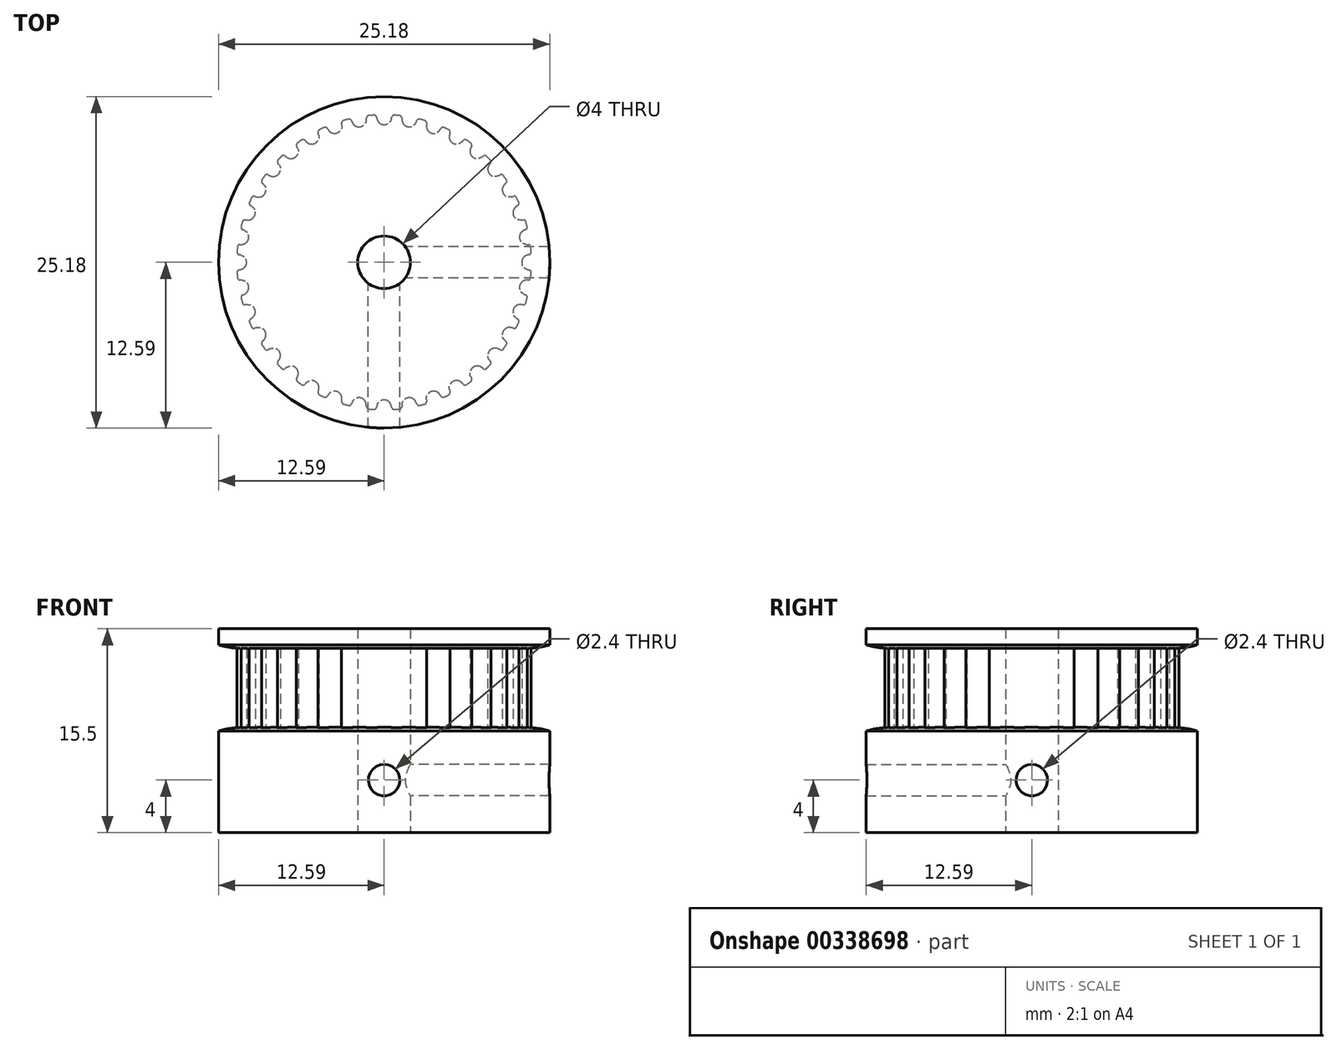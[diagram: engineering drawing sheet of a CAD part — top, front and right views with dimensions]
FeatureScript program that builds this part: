
annotation { "Feature Type Name" : "Feature", "Feature Type Description" : "" }
export const myFeature = defineFeature(function(context is Context, id is Id, definition is map)
    precondition{}
    {
        {
            assignVariable(context, id + "F0", {"name" : "teeth", "anyValue" : 36});
        }
        {
            assignVariable(context, id + "F1", {"name" : "belt_width", "anyValue" : 6 * mm});
        }
        {
            assignVariable(context, id + "F2", {"name" : "bore_diameter", "anyValue" : 4 * mm});
        }
        {
            var Q0;
            Q0=qCreatedBy(makeId("Top.planeOp"),FACE);
            var sketch = newSketch(context, id + "F3", { "sketchPlane" : qUnion([Q0])});
            skLineSegment(sketch, "E0", {"start": v(0, 0) * mm, "end": v(0, 10.46) * mm, "construction": true});
            skCircle(sketch, "E1", {"center": v(0, 0) * mm, "radius": 11.2 * mm});
            skPoint(sketch, "E2.MirrorCS.end.orphan", {"position": v(0.98, 11.16) * mm});
            skLineSegment(sketch, "E3", {"start": v(0.98, 11.16) * mm, "end": v(1, 11.42) * mm, "construction": true});
            skLineSegment(sketch, "E4", {"start": v(-0.98, 11.16) * mm, "end": v(-1, 11.42) * mm, "construction": true});
            skArc(sketch, "E5", {"start": v(0, 10.46) * mm, "mid": v(0.34, 10.57) * mm, "end": v(0.53, 10.86) * mm});
            skArc(sketch, "E6", {"start": v(0.53, 10.86) * mm, "mid": v(0.56, 10.96) * mm, "end": v(0.58, 11.05) * mm, "construction": true});
            skLineSegment(sketch, "E7", {"start": v(0, 10.46) * mm, "end": v(0, 11.2) * mm, "construction": true});
            skLineSegment(sketch, "E8", {"start": v(0, 11.2) * mm, "end": v(0, 11.46) * mm, "construction": true});
            skArc(sketch, "E9", {"start": v(0.58, 11.05) * mm, "mid": v(0.64, 11.15) * mm, "end": v(0.74, 11.18) * mm, "construction": true});
            skArc(sketch, "E10", {"start": v(1, 11.42) * mm, "mid": v(0, 11.46) * mm, "end": v(-1, 11.42) * mm, "construction": true});
            skLineSegment(sketch, "E11", {"start": v(0.98, 11.16) * mm, "end": v(0.91, 10.42) * mm});
            skLineSegment(sketch, "E12", {"start": v(0.91, 10.42) * mm, "end": v(0, 0) * mm});
            skLineSegment(sketch, "E13", {"start": v(0, 0) * mm, "end": v(-0.91, 10.42) * mm});
            skLineSegment(sketch, "E14", {"start": v(-0.91, 10.42) * mm, "end": v(-0.98, 11.16) * mm});
            skArc(sketch, "E15", {"start": v(0.78, 11.18) * mm, "mid": v(0.65, 11.14) * mm, "end": v(0.58, 11.04) * mm});
            skArc(sketch, "E16", {"start": v(0.53, 10.86) * mm, "mid": v(0.56, 10.95) * mm, "end": v(0.58, 11.04) * mm});
            skArc(sketch, "E17.MirrorCS", {"start": v(0, 10.46) * mm, "mid": v(-0.34, 10.57) * mm, "end": v(-0.53, 10.86) * mm});
            skArc(sketch, "E18.MirrorCS", {"start": v(-0.53, 10.86) * mm, "mid": v(-0.56, 10.95) * mm, "end": v(-0.58, 11.04) * mm});
            skArc(sketch, "E19.MirrorCS", {"start": v(-0.78, 11.18) * mm, "mid": v(-0.65, 11.14) * mm, "end": v(-0.58, 11.04) * mm});
            skArc(sketch, "E20", {"start": v(0, 11.2) * mm, "mid": v(-0.2, 11.2) * mm, "end": v(-0.4, 11.2) * mm});
            skArc(sketch, "E21", {"start": v(0.91, 10.42) * mm, "mid": v(0, 10.46) * mm, "end": v(-0.91, 10.42) * mm, "construction": true});
            skLineSegment(sketch, "E22", {"start": v(1, 11.42) * mm, "end": v(1.03, 11.8) * mm, "construction": true});
            skLineSegment(sketch, "E23", {"start": v(-1, 11.42) * mm, "end": v(-1.03, 11.8) * mm, "construction": true});
            skArc(sketch, "E24", {"start": v(-1.03, 11.8) * mm, "mid": v(0, 11.84) * mm, "end": v(1.03, 11.8) * mm, "construction": true});
            skSolve(sketch);
        }
        {
            var Q0;
            Q0=makeQuery(id+"F3.imprint","IMPRINT",FACE,{"disambiguationData":[TD([[makeQuery(id+"F3.imprint","IMPRINT",EDGE,{"derivedFrom":sQuery(id+"F3.wireOp",EDGE,"E5")}),-1.0]])]});
            var Q1;
            {var subQ1=sQuery(id+"F3.wireOp",EDGE,"E14");Q1=makeQuery(id+"F3.imprint","IMPRINT",FACE,{"disambiguationData":[TD([[makeQuery(id+"F3.imprint","IMPRINT",EDGE,{"derivedFrom":subQ1}),-1.0]])]});}
            var Q2;
            {var subQ0=sQuery(id+"F3.wireOp",EDGE,"E12");Q2=makeQuery(id+"F3.imprint","IMPRINT",FACE,{"disambiguationData":[TD([[makeQuery(id+"F3.imprint","IMPRINT",EDGE,{"derivedFrom":subQ0}),-1.0]])]});}
            extrude(context, id + "F4", {"entities" : qUnion([Q0, Q1, Q2]), "endBound" : BoundingType.SYMMETRIC, "depth" : getVariable(context, 'belt_width')});
        }
        {
            var Q0;
            Q0=makeQuery(id+"F4.opExtrude","SWEPT_BODY",BODY,{"disambiguationData":[OSD([sQuery(id+"F3.wireOp",EDGE,"E1"),sQuery(id+"F3.wireOp",EDGE,"E5"),sQuery(id+"F3.wireOp",EDGE,"E11"),sQuery(id+"F3.wireOp",EDGE,"E12"),sQuery(id+"F3.wireOp",EDGE,"E13"),sQuery(id+"F3.wireOp",EDGE,"E14"),sQuery(id+"F3.wireOp",EDGE,"E15"),sQuery(id+"F3.wireOp",EDGE,"E16"),sQuery(id+"F3.wireOp",EDGE,"E17.MirrorCS"),sQuery(id+"F3.wireOp",EDGE,"E18.MirrorCS"),sQuery(id+"F3.wireOp",EDGE,"E19.MirrorCS")])]});
            var Q1;
            Q1=makeQuery(id+"F4.opExtrude","SWEPT_EDGE",EDGE,{"disambiguationData":[OSD([sQuery(id+"F3.wireOp",EDGE,"E12"),sQuery(id+"F3.wireOp",EDGE,"E13")])]});
            circularPattern(context, id + "F5", {"operationType" : NewBodyOperationType.ADD, "entities" : qUnion([Q0]), "axis" : qUnion([Q1]), "angle" : 360 * degree, "instanceCount" : getVariable(context, 'teeth'), "equalSpace" : true});
        }
        {
            var Q0;
            Q0=qCreatedBy(makeId("Front.planeOp"),FACE);
            var sketch = newSketch(context, id + "F6", { "sketchPlane" : qUnion([Q0])});
            skLineSegment(sketch, "E25", {"start": v(0, -3) * mm, "end": v(11.84, -3) * mm});
            skLineSegment(sketch, "E26", {"start": v(11.84, -3) * mm, "end": v(12.6, -3.28) * mm});
            skLineSegment(sketch, "E27", {"start": v(12.6, -3.28) * mm, "end": v(12.6, -11) * mm});
            skLineSegment(sketch, "E28", {"start": v(12.6, -11) * mm, "end": v(0, -11) * mm});
            skLineSegment(sketch, "E29", {"start": v(0, -11) * mm, "end": v(0, -3) * mm});
            skLineSegment(sketch, "E30", {"start": v(0, 3) * mm, "end": v(11.84, 3) * mm});
            skLineSegment(sketch, "E31", {"start": v(12.6, 3.28) * mm, "end": v(11.84, 3) * mm});
            skLineSegment(sketch, "E32", {"start": v(12.6, 3.28) * mm, "end": v(12.6, 4.5) * mm});
            skLineSegment(sketch, "E33", {"start": v(12.6, 4.5) * mm, "end": v(0, 4.5) * mm});
            skLineSegment(sketch, "E34", {"start": v(0, 4.5) * mm, "end": v(0, 3) * mm});
            skLineSegment(sketch, "E35", {"start": v(11.84, -3) * mm, "end": v(12.6, -3) * mm, "construction": true});
            skLineSegment(sketch, "E36", {"start": v(12.6, -3) * mm, "end": v(12.6, -3.28) * mm, "construction": true});
            skLineSegment(sketch, "E37", {"start": v(11.84, 3) * mm, "end": v(12.6, 3) * mm, "construction": true});
            skLineSegment(sketch, "E38", {"start": v(12.6, 3) * mm, "end": v(12.6, 3.28) * mm, "construction": true});
            skLineSegment(sketch, "E39", {"start": v(11.2, 0) * mm, "end": v(11.2, -3) * mm, "construction": true});
            skSolve(sketch);
        }
        {
            var Q0;
            Q0=qSketchRegion(id+"F6",true);
            var Q1;
            Q1=qConstructionFilter(qBodyType(qCreatedBy(id+"F6",EDGE),BodyType.WIRE),ConstructionObject.NO);
            var Q2;
            Q2=sQuery(id+"F6.wireOp",EDGE,"E29");
            revolve(context, id + "F7", {"operationType" : NewBodyOperationType.ADD, "entities" : qUnion([Q0]), "surfaceEntities" : qUnion([Q1]), "axis" : qUnion([Q2]), "revolveType" : RevolveType.FULL});
        }
        {
            var Q0;
            Q0=makeQuery(id+"F7.opRevolve","SWEPT_FACE",FACE,{"disambiguationData":[OSD([sQuery(id+"F6.wireOp",EDGE,"E28")])]});
            var sketch = newSketch(context, id + "F8", { "sketchPlane" : qUnion([Q0])});
            skPoint(sketch, "E40", {"position": v(0, 0) * mm});
            skSolve(sketch);
        }
        {
            var Q0;
            Q0=sQuery(id+"F8.wireOp",VERTEX,"E40");
            var Q1;
            Q1=makeQuery(id+"F4.opExtrude","SWEPT_BODY",BODY,{"disambiguationData":[OSD([sQuery(id+"F3.wireOp",EDGE,"E1"),sQuery(id+"F3.wireOp",EDGE,"E5"),sQuery(id+"F3.wireOp",EDGE,"E11"),sQuery(id+"F3.wireOp",EDGE,"E12"),sQuery(id+"F3.wireOp",EDGE,"E13"),sQuery(id+"F3.wireOp",EDGE,"E14"),sQuery(id+"F3.wireOp",EDGE,"E15"),sQuery(id+"F3.wireOp",EDGE,"E16"),sQuery(id+"F3.wireOp",EDGE,"E17.MirrorCS"),sQuery(id+"F3.wireOp",EDGE,"E18.MirrorCS"),sQuery(id+"F3.wireOp",EDGE,"E19.MirrorCS")])]});
            hole(context, id + "F9", {"style" : HoleStyle.SIMPLE, "holeDiameter" : getVariable(context, 'bore_diameter'), "endStyle" : HoleEndStyle.THROUGH, "locations" : qUnion([Q0]), "scope" : qUnion([Q1]), "isTappedThrough" : true});
        }
        {
            var Q0;
            Q0=qCreatedBy(makeId("Front.planeOp"),FACE);
            var sketch = newSketch(context, id + "F10", { "sketchPlane" : qUnion([Q0])});
            skPoint(sketch, "E41", {"position": v(0, -7) * mm});
            skLineSegment(sketch, "E42", {"start": v(0, -11) * mm, "end": v(0, -3) * mm});
            skSolve(sketch);
        }
        {
            var Q0;
            Q0=qCreatedBy(makeId("Right.planeOp"),FACE);
            var sketch = newSketch(context, id + "F11", { "sketchPlane" : qUnion([Q0])});
            skPoint(sketch, "E43", {"position": v(0, -7) * mm});
            skSolve(sketch);
        }
        {
            var Q0;
            Q0=sQuery(id+"F10.wireOp",VERTEX,"E41");
            var Q1;
            Q1=makeQuery(id+"F4.opExtrude","SWEPT_BODY",BODY,{"disambiguationData":[OSD([sQuery(id+"F3.wireOp",EDGE,"E1"),sQuery(id+"F3.wireOp",EDGE,"E5"),sQuery(id+"F3.wireOp",EDGE,"E11"),sQuery(id+"F3.wireOp",EDGE,"E12"),sQuery(id+"F3.wireOp",EDGE,"E13"),sQuery(id+"F3.wireOp",EDGE,"E14"),sQuery(id+"F3.wireOp",EDGE,"E15"),sQuery(id+"F3.wireOp",EDGE,"E16"),sQuery(id+"F3.wireOp",EDGE,"E17.MirrorCS"),sQuery(id+"F3.wireOp",EDGE,"E18.MirrorCS"),sQuery(id+"F3.wireOp",EDGE,"E19.MirrorCS")])]});
            hole(context, id + "F12", {"style" : HoleStyle.SIMPLE, "endStyle" : HoleEndStyle.THROUGH, "oppositeDirection" : true, "standardTappedOrClearance" : lookupTablePath({ "standard" : "ISO", "engagement" : "75%", "pitch" : "0.6 mm", "size" : "M3", "type" : "Tapped" }), "standardBlindInLast" : lookupTablePath({ "standard" : "ISO", "engagement" : "75%", "pitch" : "0.6 mm", "size" : "M3", "type" : "Tapped" }), "holeDiameter" : 2.4 * mm, "locations" : qUnion([Q0]), "scope" : qUnion([Q1]), "isTappedThrough" : true, "showTappedDepth" : true});
        }
        {
            var Q0;
            Q0=sQuery(id+"F11.wireOp",VERTEX,"E43");
            var Q1;
            Q1=makeQuery(id+"F4.opExtrude","SWEPT_BODY",BODY,{"disambiguationData":[OSD([sQuery(id+"F3.wireOp",EDGE,"E1"),sQuery(id+"F3.wireOp",EDGE,"E5"),sQuery(id+"F3.wireOp",EDGE,"E11"),sQuery(id+"F3.wireOp",EDGE,"E12"),sQuery(id+"F3.wireOp",EDGE,"E13"),sQuery(id+"F3.wireOp",EDGE,"E14"),sQuery(id+"F3.wireOp",EDGE,"E15"),sQuery(id+"F3.wireOp",EDGE,"E16"),sQuery(id+"F3.wireOp",EDGE,"E17.MirrorCS"),sQuery(id+"F3.wireOp",EDGE,"E18.MirrorCS"),sQuery(id+"F3.wireOp",EDGE,"E19.MirrorCS")])]});
            hole(context, id + "F13", {"style" : HoleStyle.SIMPLE, "endStyle" : HoleEndStyle.THROUGH, "oppositeDirection" : true, "standardTappedOrClearance" : lookupTablePath({ "standard" : "ISO", "engagement" : "75%", "pitch" : "0.6 mm", "size" : "M3", "type" : "Tapped" }), "standardBlindInLast" : lookupTablePath({ "standard" : "ISO", "engagement" : "75%", "pitch" : "0.6 mm", "size" : "M3", "type" : "Tapped" }), "holeDiameter" : 2.4 * mm, "locations" : qUnion([Q0]), "scope" : qUnion([Q1]), "isTappedThrough" : true, "showTappedDepth" : true});
        }
        {
            var Q0;
            Q0=makeQuery(id+"F7.opRevolve","SWEPT_EDGE",EDGE,{"disambiguationData":[OSD([sQuery(id+"F6.wireOp",EDGE,"E25"),sQuery(id+"F6.wireOp",EDGE,"E26")])]});
            fillet(context, id + "F14", {"entities" : qUnion([Q0]), "radius" : 7 * mm, "tangentPropagation" : true, "allowEdgeOverflow" : false});
        }
        {
            var Q0;
            Q0=makeQuery(id+"F7.opRevolve","SWEPT_EDGE",EDGE,{"disambiguationData":[OSD([sQuery(id+"F6.wireOp",EDGE,"E30"),sQuery(id+"F6.wireOp",EDGE,"E31")])]});
            fillet(context, id + "F15", {"entities" : qUnion([Q0]), "radius" : 7 * mm, "tangentPropagation" : true, "allowEdgeOverflow" : false});
        }
    });
